# Revit family: Mechanical_Air-Curtain_Ready-Access_Fly-Fan
name_source: partatom
category: Mechanical Equipment
units: mm (PartAtom-declared; Revit-internal decimal feet)

## family parameters
Classification Number = 23.75.70.21.17
Cut with Voids When Loaded = No
Host = Face
Maintain Annotation Orientation = No
Part Type = Normal
Room Calculation Point = No
Round Connector Dimension = Use Diameter
Shared = No

## types (6) — shared parameters
Assembly Code = D3090400
Construction Details = http://www.arcat.com
Default Elevation = 0' - 0"
Electrical_Frequency = 60 Hz
HVAC_Outlet Velocity = 600 FPM
Keynote = 08582
Manufacturer = Ready Access
Manufacturer Fax = 630-876-7767
Manufacturer Website = http://www.ready-access.com
Product Data = http://www.arcat.com
Revision = R1_2014-09
Sales Information = http://www.ready-access.com
Send Message = http://www.arcat.com
Specification = http://www.arcat.com
URL = http://www.ready-access.com
zero-valued in all types: Expected Lifespan (Years), Maintenance Schedule (Months), Warranty Duration (Years)

## per-type parameters (varying)
| type | 2 Panel Window | BiPart Panel Window | Description | Electrical_Amperage | Electrical_Voltage | Frame Depth | Jamb Thickness | Model | Unit Height | Unit Width |
| For 600 Series International | Yes | No | Ready Access Air Curtain Transom - Fly Fan for 600 Series as Specified | 3 A | 240 V | 0' - 4 1/2" | 0' - 2" | AA100-600 | 1' - 1 1/2" | 3' - 11 1/2" |
| For 600 Series Domestic | Yes | No | Ready Access Air Curtain Transom - Fly Fan for 600 Series as Specified | 3 A | 115 V | 0' - 4 1/2" | 0' - 2" | AA100-600 | 1' - 1 1/2" | 3' - 11 1/2" |
| For 275 Series International | Yes | No | Ready Access Air Curtain Transom - Fly Fan for 275 Series as Specified | 3 A | 240 V | 0' - 4" | 0' - 1 3/4" | AA100-275 | 1' - 1 1/2" | 3' - 11 1/2" |
| For 275 Series Domestic | Yes | No | Ready Access Air Curtain Transom - Fly Fan for 275 Series as Specified | 3 A | 115 V | 0' - 4" | 0' - 1 3/4" | AA100-275 | 1' - 1 1/2" | 3' - 11 1/2" |
| For 131 Series International | No | Yes | Ready Access Air Curtain Transom - Fly Fan for 131 Series as Specified | 8 A | 240 V | 0' - 4" | 0' - 1 3/4" | AA100-131 | 1' - 1 3/4" | 4' - 5 1/2" |
| For 131 Series Domestic | No | Yes | Ready Access Air Curtain Transom - Fly Fan for 131 Series as Specified | 15 A | 115 V | 0' - 4" | 0' - 1 3/4" | AA100-131 | 1' - 1 3/4" | 4' - 5 1/2" |

## geometry (parser evidence)
native form markers: Sweep x2
no freeform markers — native parametric forms only
